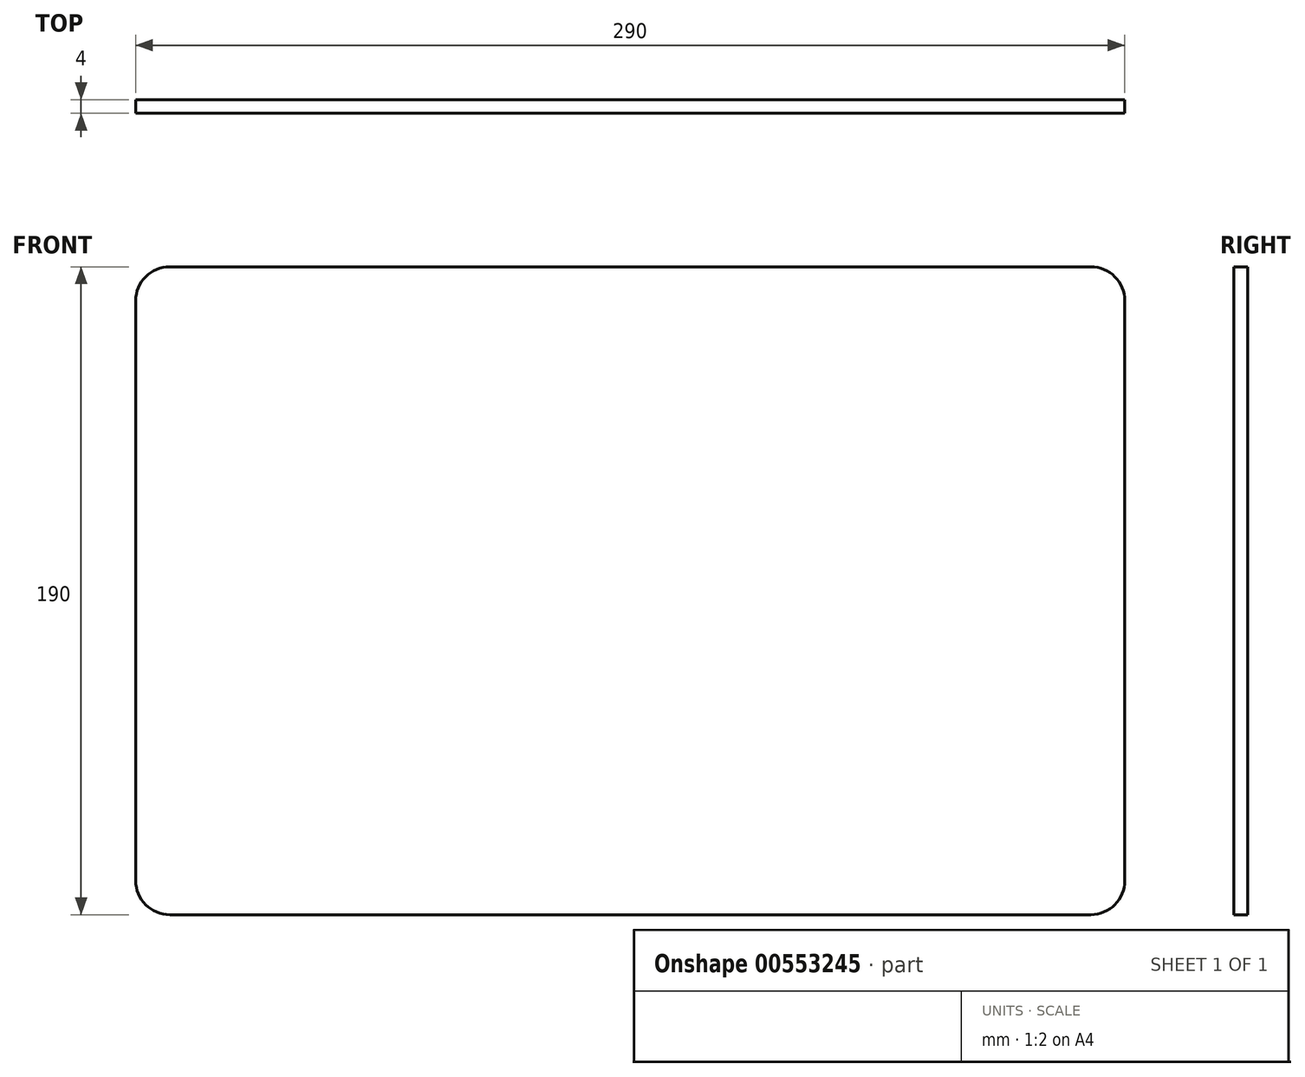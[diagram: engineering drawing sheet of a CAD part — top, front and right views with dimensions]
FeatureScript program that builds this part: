
annotation { "Feature Type Name" : "Feature", "Feature Type Description" : "" }
export const myFeature = defineFeature(function(context is Context, id is Id, definition is map)
    precondition{}
    {
        {
            var Q0;
            Q0=qCreatedBy(makeId("Front.planeOp"),FACE);
            var sketch = newSketch(context, id + "F0", { "sketchPlane" : qUnion([Q0])});
            skPoint(sketch, "E0.middle", {"position": v(0, 0) * mm});
            skArc(sketch, "E1", {"start": v(-135, -95) * mm, "mid": v(-142.07, -92.07) * mm, "end": v(-145, -85) * mm});
            skArc(sketch, "E2", {"start": v(-145, 85) * mm, "mid": v(-142.07, 92.07) * mm, "end": v(-135, 95) * mm});
            skArc(sketch, "E3", {"start": v(135, 95) * mm, "mid": v(142.07, 92.07) * mm, "end": v(145, 85) * mm});
            skArc(sketch, "E4", {"start": v(145, -85) * mm, "mid": v(142.07, -92.07) * mm, "end": v(135, -95) * mm});
            skLineSegment(sketch, "E5", {"start": v(135, -95) * mm, "end": v(-135, -95) * mm});
            skLineSegment(sketch, "E6", {"start": v(-145, -85) * mm, "end": v(-145, 85) * mm});
            skLineSegment(sketch, "E7", {"start": v(-135, 95) * mm, "end": v(135, 95) * mm});
            skLineSegment(sketch, "E8", {"start": v(145, 85) * mm, "end": v(145, -85) * mm});
            skSolve(sketch);
        }
        {
            var Q0;
            Q0 = qSketchRegion(id + "F0", true);
            extrude(context, id + "F1", {"entities" : qUnion([Q0]), "depth" : 4 * mm, "offsetDistance" : 25 * mm});
        }
    });
